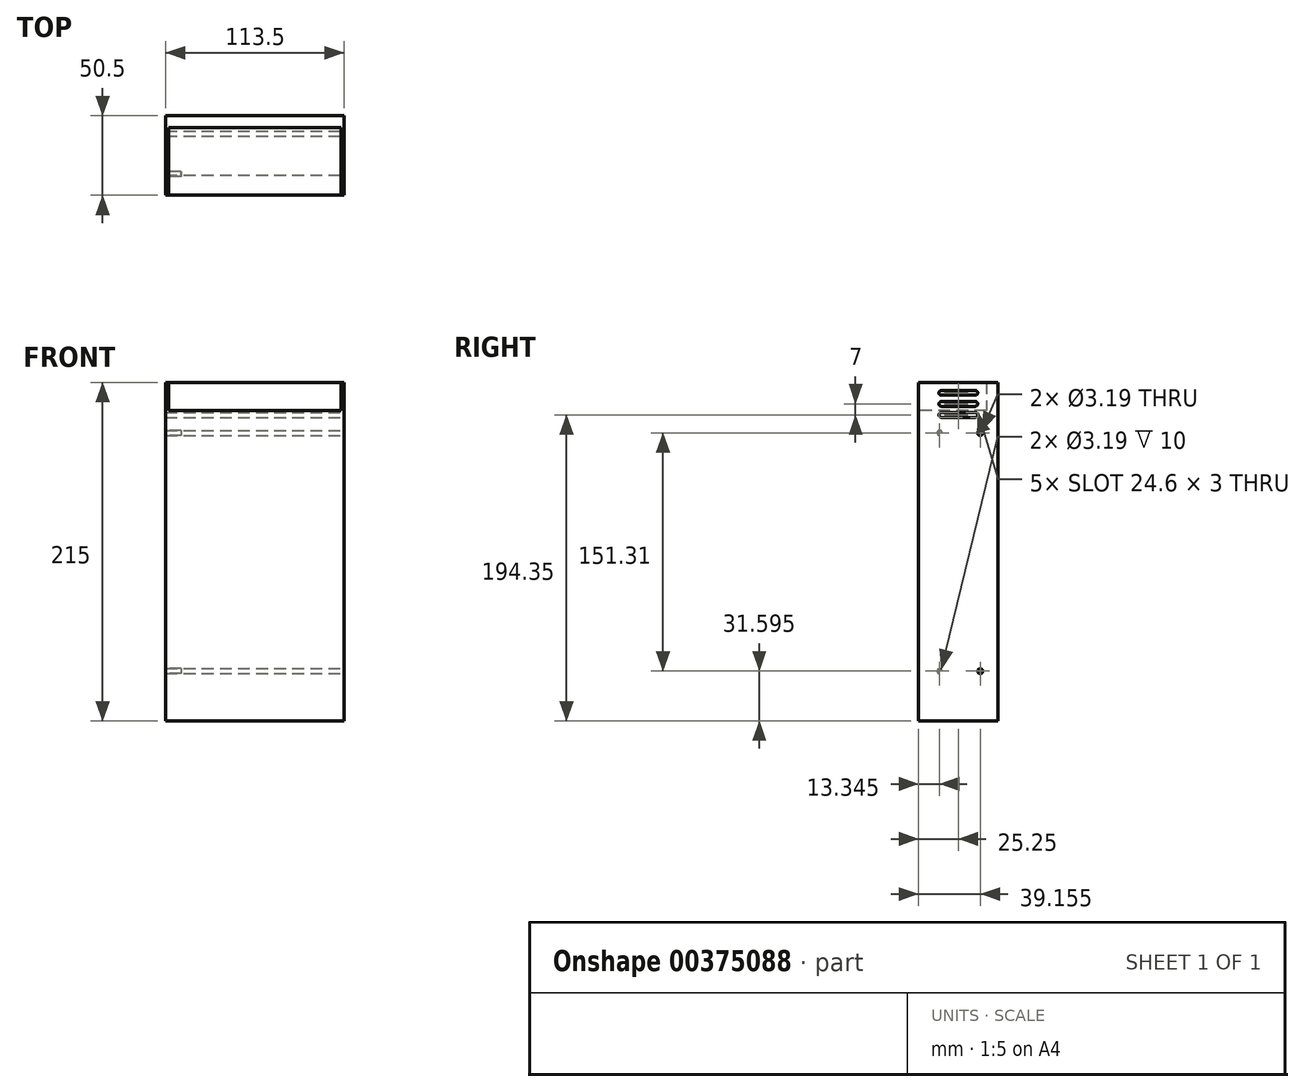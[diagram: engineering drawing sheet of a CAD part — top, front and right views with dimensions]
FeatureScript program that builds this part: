
annotation { "Feature Type Name" : "Feature", "Feature Type Description" : "" }
export const myFeature = defineFeature(function(context is Context, id is Id, definition is map)
    precondition{}
    {
        {
            var Q0;
            Q0=qCreatedBy(makeId("Top.planeOp"),FACE);
            var sketch = newSketch(context, id + "F0", { "sketchPlane" : qUnion([Q0])});
            skLineSegment(sketch, "E0.bottom", {"start": v(0, 0) * mm, "end": v(113.5, 0) * mm});
            skLineSegment(sketch, "E0.top", {"start": v(0, 50.5) * mm, "end": v(113.5, 50.5) * mm});
            skLineSegment(sketch, "E0.left", {"start": v(0, 0) * mm, "end": v(0, 50.5) * mm});
            skLineSegment(sketch, "E0.right", {"start": v(113.5, 0) * mm, "end": v(113.5, 50.5) * mm});
            skSolve(sketch);
        }
        {
            var Q0;
            Q0=qSketchRegion(id+"F0",true);
            extrude(context, id + "F1", {"entities" : qUnion([Q0]), "depth" : 215 * mm});
        }
        {
            var Q0;
            Q0=makeQuery(id+"F1.opExtrude","SWEPT_FACE",FACE,{"disambiguationData":[OSD([sQuery(id+"F0.wireOp",EDGE,"E0.right")])]});
            var sketch = newSketch(context, id + "F2", { "sketchPlane" : qUnion([Q0])});
            skLineSegment(sketch, "E1.bottom", {"start": v(14.45, 209.85) * mm, "end": v(36.05, 209.85) * mm});
            skLineSegment(sketch, "E1.top", {"start": v(14.45, 206.85) * mm, "end": v(36.05, 206.85) * mm});
            skLineSegment(sketch, "E1.left", {"start": v(12.95, 208.35) * mm, "end": v(12.95, 208.35) * mm});
            skLineSegment(sketch, "E1.right", {"start": v(37.55, 208.35) * mm, "end": v(37.55, 208.35) * mm});
            skPoint(sketch, "E2.visualSharp", {"position": v(12.95, 209.85) * mm});
            skArc(sketch, "E2.filletArc", {"start": v(14.45, 209.85) * mm, "mid": v(13.39, 209.41) * mm, "end": v(12.95, 208.35) * mm});
            skPoint(sketch, "E3.visualSharp", {"position": v(12.95, 206.85) * mm});
            skArc(sketch, "E3.filletArc", {"start": v(12.95, 208.35) * mm, "mid": v(13.39, 207.29) * mm, "end": v(14.45, 206.85) * mm});
            skPoint(sketch, "E4.visualSharp", {"position": v(37.55, 209.85) * mm});
            skArc(sketch, "E4.filletArc", {"start": v(37.55, 208.35) * mm, "mid": v(37.11, 209.41) * mm, "end": v(36.05, 209.85) * mm});
            skPoint(sketch, "E5.visualSharp", {"position": v(37.55, 206.85) * mm});
            skArc(sketch, "E5.filletArc", {"start": v(36.05, 206.85) * mm, "mid": v(37.11, 207.29) * mm, "end": v(37.55, 208.35) * mm});
            skPoint(sketch, "E6.1.0.0", {"position": v(37.55, 199.85) * mm});
            skPoint(sketch, "E6.1.0.1", {"position": v(12.95, 202.85) * mm});
            skPoint(sketch, "E6.1.0.2", {"position": v(37.55, 202.85) * mm});
            skLineSegment(sketch, "E6.1.0.3", {"start": v(14.45, 199.85) * mm, "end": v(36.05, 199.85) * mm});
            skLineSegment(sketch, "E6.1.0.4", {"start": v(14.45, 202.85) * mm, "end": v(36.05, 202.85) * mm});
            skPoint(sketch, "E6.1.0.5", {"position": v(12.95, 199.85) * mm});
            skArc(sketch, "E6.1.0.6", {"start": v(12.95, 201.35) * mm, "mid": v(13.39, 200.29) * mm, "end": v(14.45, 199.85) * mm});
            skArc(sketch, "E6.1.0.7", {"start": v(37.55, 201.35) * mm, "mid": v(37.11, 202.41) * mm, "end": v(36.05, 202.85) * mm});
            skArc(sketch, "E6.1.0.8", {"start": v(36.05, 199.85) * mm, "mid": v(37.11, 200.29) * mm, "end": v(37.55, 201.35) * mm});
            skArc(sketch, "E6.1.0.9", {"start": v(14.45, 202.85) * mm, "mid": v(13.39, 202.41) * mm, "end": v(12.95, 201.35) * mm});
            skPoint(sketch, "E6.2.0.0", {"position": v(37.55, 192.85) * mm});
            skPoint(sketch, "E6.2.0.1", {"position": v(12.95, 195.85) * mm});
            skPoint(sketch, "E6.2.0.2", {"position": v(37.55, 195.85) * mm});
            skLineSegment(sketch, "E6.2.0.3", {"start": v(14.45, 192.85) * mm, "end": v(36.05, 192.85) * mm});
            skLineSegment(sketch, "E6.2.0.4", {"start": v(14.45, 195.85) * mm, "end": v(36.05, 195.85) * mm});
            skPoint(sketch, "E6.2.0.5", {"position": v(12.95, 192.85) * mm});
            skArc(sketch, "E6.2.0.6", {"start": v(12.95, 194.35) * mm, "mid": v(13.39, 193.29) * mm, "end": v(14.45, 192.85) * mm});
            skArc(sketch, "E6.2.0.7", {"start": v(37.55, 194.35) * mm, "mid": v(37.11, 195.41) * mm, "end": v(36.05, 195.85) * mm});
            skArc(sketch, "E6.2.0.8", {"start": v(36.05, 192.85) * mm, "mid": v(37.11, 193.29) * mm, "end": v(37.55, 194.35) * mm});
            skArc(sketch, "E6.2.0.9", {"start": v(14.45, 195.85) * mm, "mid": v(13.39, 195.41) * mm, "end": v(12.95, 194.35) * mm});
            skLineSegment(sketch, "E6.direction1", {"start": v(12.95, 206.85) * mm, "end": v(12.95, 199.85) * mm, "construction": true});
            skSolve(sketch);
        }
        {
            var Q0;
            Q0=makeQuery(id+"F2.imprint","IMPRINT",FACE,{"disambiguationData":[TD([[makeQuery(id+"F2.imprint","IMPRINT",EDGE,{"derivedFrom":sQuery(id+"F2.wireOp",EDGE,"E1.bottom")}),-1.0]])]});
            var Q1;
            Q1=makeQuery(id+"F2.imprint","IMPRINT",FACE,{"disambiguationData":[TD([[makeQuery(id+"F2.imprint","IMPRINT",EDGE,{"derivedFrom":sQuery(id+"F2.wireOp",EDGE,"E6.1.0.3")}),1.0]])]});
            var Q2;
            Q2=makeQuery(id+"F2.imprint","IMPRINT",FACE,{"disambiguationData":[TD([[makeQuery(id+"F2.imprint","IMPRINT",EDGE,{"derivedFrom":sQuery(id+"F2.wireOp",EDGE,"E6.2.0.3")}),1.0]])]});
            extrude(context, id + "F3", {"entities" : qUnion([Q0, Q1, Q2]), "operationType" : NewBodyOperationType.REMOVE, "endBound" : BoundingType.THROUGH_ALL, "oppositeDirection" : true, "depth" : 25 * mm});
        }
        {
            var Q0;
            Q0=makeQuery(id+"F1.opExtrude","SWEPT_FACE",FACE,{"disambiguationData":[OSD([sQuery(id+"F0.wireOp",EDGE,"E0.bottom")])]});
            var sketch = newSketch(context, id + "F4", { "sketchPlane" : qUnion([Q0])});
            skLineSegment(sketch, "E7", {"start": v(111.5, 215) * mm, "end": v(111.5, 197) * mm});
            skLineSegment(sketch, "E8", {"start": v(2, 215) * mm, "end": v(2, 197) * mm});
            skLineSegment(sketch, "E9", {"start": v(2, 197) * mm, "end": v(111.5, 197) * mm});
            skSolve(sketch);
        }
        {
            var Q0;
            {var subQ0=sQuery(id+"F4.wireOp",EDGE,"E7");Q0=makeQuery(id+"F4.imprint","IMPRINT",FACE,{"disambiguationData":[TD([[makeQuery(id+"F4.imprint","IMPRINT",EDGE,{"derivedFrom":subQ0}),-1.0]])]});}
            extrude(context, id + "F5", {"entities" : qUnion([Q0]), "operationType" : NewBodyOperationType.REMOVE, "oppositeDirection" : true, "depth" : (50.5 - 7.5) * mm});
        }
        {
            var Q0;
            Q0=makeQuery(id+"F1.opExtrude","SWEPT_FACE",FACE,{"disambiguationData":[OSD([sQuery(id+"F0.wireOp",EDGE,"E0.right")])]});
            var sketch = newSketch(context, id + "F6", { "sketchPlane" : qUnion([Q0])});
            skCircle(sketch, "E10", {"center": v(39.15, 182.9) * mm, "radius": 1.6 * mm});
            skCircle(sketch, "E11", {"center": v(39.15, 31.6) * mm, "radius": 1.6 * mm});
            skSolve(sketch);
        }
        {
            var Q0;
            Q0=makeQuery(id+"F6.imprint","IMPRINT",FACE,{"disambiguationData":[TD([[makeQuery(id+"F6.imprint","IMPRINT",EDGE,{"derivedFrom":sQuery(id+"F6.wireOp",EDGE,"E11")}),1.0]])]});
            var Q1;
            Q1=makeQuery(id+"F6.imprint","IMPRINT",FACE,{"disambiguationData":[TD([[makeQuery(id+"F6.imprint","IMPRINT",EDGE,{"derivedFrom":sQuery(id+"F6.wireOp",EDGE,"E10")}),1.0]])]});
            extrude(context, id + "F7", {"entities" : qUnion([Q0, Q1]), "operationType" : NewBodyOperationType.REMOVE, "endBound" : BoundingType.THROUGH_ALL, "oppositeDirection" : true, "depth" : 10 * mm});
        }
        {
            var Q0;
            Q0=makeQuery(id+"F1.opExtrude","SWEPT_FACE",FACE,{"disambiguationData":[OSD([sQuery(id+"F0.wireOp",EDGE,"E0.left")])]});
            var sketch = newSketch(context, id + "F8", { "sketchPlane" : qUnion([Q0])});
            skCircle(sketch, "E12", {"center": v(-13.34, 182.9) * mm, "radius": 1.6 * mm});
            skCircle(sketch, "E13", {"center": v(-13.34, 31.6) * mm, "radius": 1.6 * mm});
            skSolve(sketch);
        }
        {
            var Q0;
            Q0=qSketchRegion(id+"F8",true);
            extrude(context, id + "F9", {"entities" : qUnion([Q0]), "operationType" : NewBodyOperationType.REMOVE, "oppositeDirection" : true, "depth" : 10 * mm});
        }
    });
